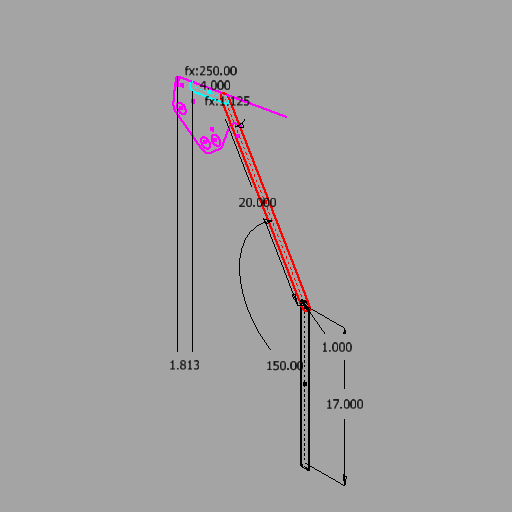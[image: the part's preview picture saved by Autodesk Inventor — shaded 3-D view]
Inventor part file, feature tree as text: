
AUTODESK INVENTOR PART (.ipt)
format: ipt  version: 2024.2 (Build 282272000, 272)  size: 293,376 bytes
history: native  units: in
note: dims shown in document units (in); Inventor stores cm internally (conversion verified against a paired STEP export)
features: other x2, sketch x1
ambient origin geometry x8: Origin, YZ Plane, XZ Plane, XY Plane, X Axis, Y Axis, Z Axis, Center Point
feature tree (3):
  other  "Blocks"
  sketch  "Sketch1"  dims[d0=17.0in d1=1.0in d2=20.0in d3=1.125in d4=4.0in d6=1.7178in d8=1.8126in]
  other  "Block1:1"
